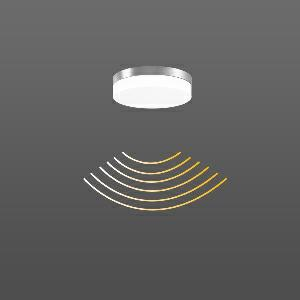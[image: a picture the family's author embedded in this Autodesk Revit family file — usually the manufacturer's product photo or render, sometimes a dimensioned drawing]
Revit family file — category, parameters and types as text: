
# Revit family: flat_slim_round_312135_004_191_7694
name_source: partatom
category: Lighting Fixtures
units: mm (PartAtom-declared; Revit-internal decimal feet)

## family parameters
Cut with Voids When Loaded = No
Host = Face
Light Source = No
Part Type = Normal
Room Calculation Point = No
Round Connector Dimension = Use Diameter
Shared = No

## types (1)
- FLAT SLIM round (1 x LED Modul 830, 1150 lm, 3000)
    Apparent Load = 13 VA
    CIE Flux Codes = 43 74 92 91 100
    Color Rendering = 80
    Color Temperature = 3000
    Default Elevation = 1800 mm
    Height = 63 mm
    Lamp = 1 x LED Modul 830
    Lamp Light Flux = 1150 lm
    Lamp count = 1
    Length = 230 mm
    Lifetime = 50000 h
    Luminous efficacy = 88 lm/W
    Manufacturer = RZB
    ModVariant = No
    Model = 312135.004.191
    Mounting Place = Ceiling, Wall
    Mounting Type = Surface mounted
    Number of Poles = 1
    OnlyDefault = Yes
    Power Factor = 1
    Product Name = FLAT SLIM round
    Product group = Surface mounted ceiling and wall luminaires
    ProductGroupID = 305
    Protection Class = Protection class I
    Protection Degree = IP 65
    RLX_Detail_Level = 1
    RLX_Emergency_Light_Flux = 0 lm
    RLX_Emergency_Type = 0
    RLX_Emergency_Type_DB = No
    RlxData = <blob elided: 31505 chars, md5=0234dad2>
    Socket = socket
    Standby Power = 0 W
    System Light Flux = 1150 lm
    System Power = 13 W
    Type Comments = Product without accessories
    Type Image = 312132.004.19.jpg
    URL = http://relux.com
    VarID = ---
    Voltage = 230 V
    Voltage Range = 220-240 V
    Weight = 0.00 kg
    Width = 0 mm  [stored 0 ft]

note: [stored X ft] marks values corroborated as IEEE doubles in the binary element streams (Revit-internal decimal feet)

## geometry (parser evidence)
native form markers: Blend x4, Sweep x12
no freeform markers — native parametric forms only
